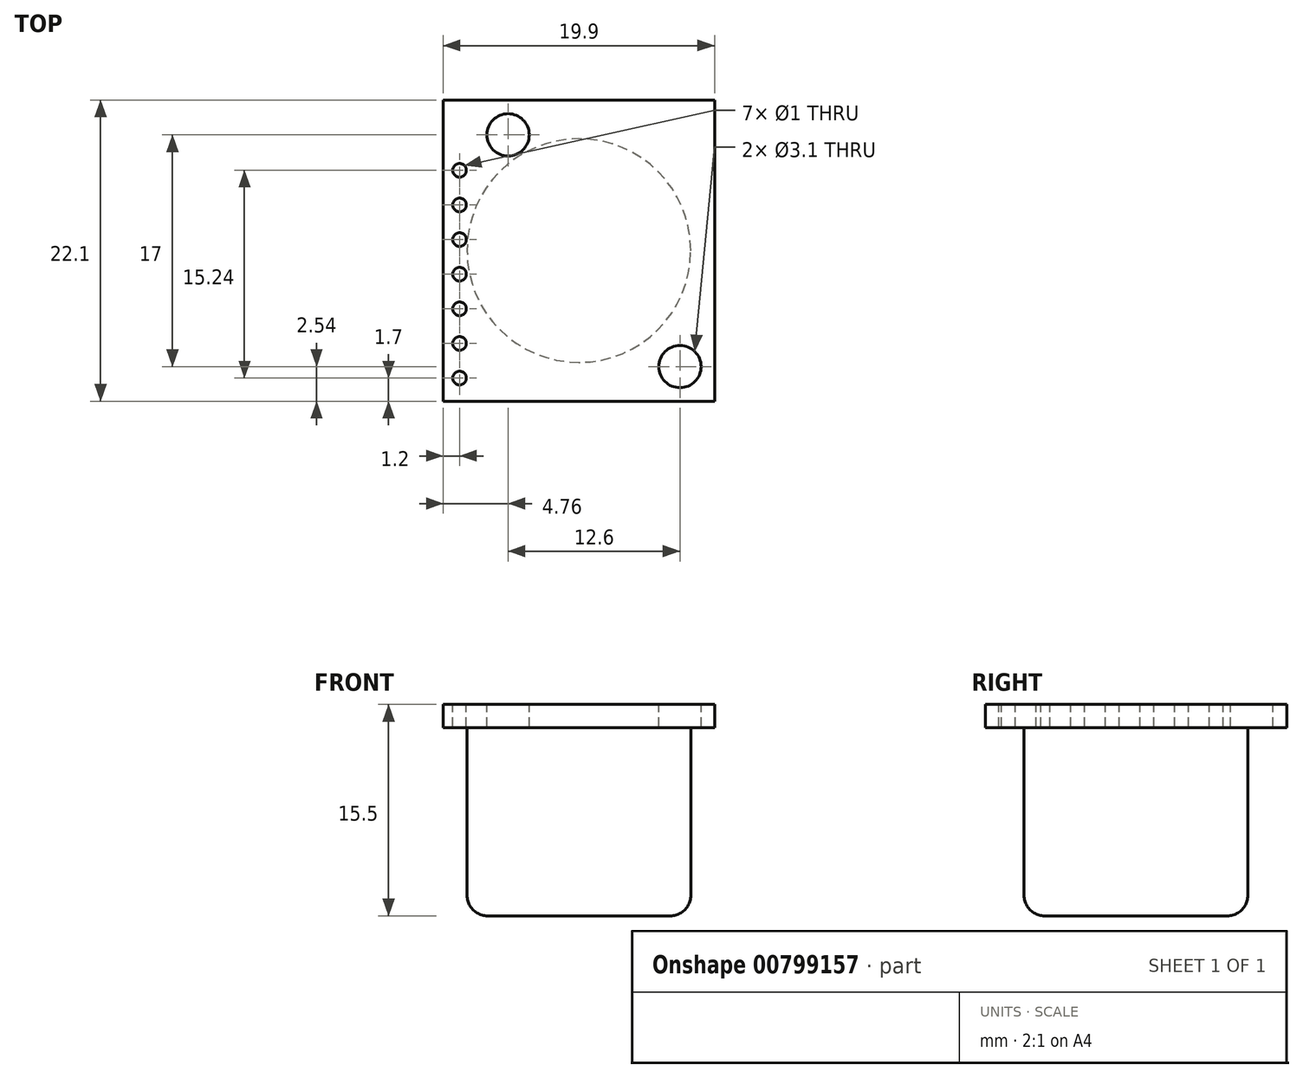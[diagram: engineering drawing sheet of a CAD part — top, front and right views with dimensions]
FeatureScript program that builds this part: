
annotation { "Feature Type Name" : "Feature", "Feature Type Description" : "" }
export const myFeature = defineFeature(function(context is Context, id is Id, definition is map)
    precondition{}
    {
        {
            var Q0;
            Q0=qCreatedBy(makeId("Top.planeOp"),FACE);
            var sketch = newSketch(context, id + "F0", { "sketchPlane" : qUnion([Q0])});
            skLineSegment(sketch, "E0.bottom", {"start": v(-9.95, 11.05) * mm, "end": v(9.95, 11.05) * mm});
            skLineSegment(sketch, "E0.top", {"start": v(-9.95, -11.05) * mm, "end": v(9.95, -11.05) * mm});
            skLineSegment(sketch, "E0.left", {"start": v(-9.95, 11.05) * mm, "end": v(-9.95, -11.05) * mm});
            skLineSegment(sketch, "E0.right", {"start": v(9.95, 11.05) * mm, "end": v(9.95, -11.05) * mm});
            skPoint(sketch, "E0.middle", {"position": v(0, 0) * mm});
            skPoint(sketch, "E1", {"position": v(7.41, -8.5) * mm});
            skPoint(sketch, "E2", {"position": v(-5.2, 8.5) * mm});
            skPoint(sketch, "E3", {"position": v(-8.75, -9.35) * mm});
            skPoint(sketch, "E4.0.1.0", {"position": v(-8.75, -6.81) * mm});
            skPoint(sketch, "E4.0.2.0", {"position": v(-8.75, -4.27) * mm});
            skPoint(sketch, "E4.0.3.0", {"position": v(-8.75, -1.73) * mm});
            skPoint(sketch, "E4.0.4.0", {"position": v(-8.75, 0.81) * mm});
            skPoint(sketch, "E4.0.5.0", {"position": v(-8.75, 3.35) * mm});
            skPoint(sketch, "E4.0.6.0", {"position": v(-8.75, 5.9) * mm});
            skLineSegment(sketch, "E4.direction1", {"start": v(-8.75, -9.35) * mm, "end": v(-8.75, -9.35) * mm});
            skLineSegment(sketch, "E4.direction2", {"start": v(-8.75, -9.35) * mm, "end": v(-8.75, -6.81) * mm, "construction": true});
            skSolve(sketch);
        }
        {
            var Q0;
            Q0=makeQuery(id+"F0.imprint","IMPRINT",FACE,{"disambiguationData":[TD([[makeQuery(id+"F0.imprint","IMPRINT",EDGE,{"derivedFrom":sQuery(id+"F0.wireOp",EDGE,"E0.bottom")}),-1.0]])]});
            extrude(context, id + "F1", {"entities" : qUnion([Q0]), "oppositeDirection" : true, "depth" : 1.7 * mm, "offsetDistance" : 25 * mm});
        }
        {
            var Q0;
            Q0=sQuery(id+"F0.wireOp",VERTEX,"E2");
            var Q1;
            Q1=sQuery(id+"F0.wireOp",VERTEX,"E1");
            var Q2;
            Q2=makeQuery(id+"F1.opExtrude","SWEPT_BODY",BODY,{"disambiguationData":[OSD([sQuery(id+"F0.wireOp",EDGE,"E0.bottom"),sQuery(id+"F0.wireOp",EDGE,"E0.top"),sQuery(id+"F0.wireOp",EDGE,"E0.left"),sQuery(id+"F0.wireOp",EDGE,"E0.right")])]});
            hole(context, id + "F2", {"style" : HoleStyle.SIMPLE, "endStyle" : HoleEndStyle.BLIND, "holeDiameter" : 3.1 * mm, "majorDiameter" : 5 * mm, "holeDepth" : 5 * mm, "isTappedThrough" : true, "tappedDepth" : 12 * mm, "tapClearance" : 3, "locations" : qUnion([Q0, Q1]), "scope" : qUnion([Q2])});
        }
        {
            var Q0;
            Q0=sQuery(id+"F0.wireOp",VERTEX,"E4.0.6.0");
            var Q1;
            Q1=sQuery(id+"F0.wireOp",VERTEX,"E4.0.5.0");
            var Q2;
            Q2=sQuery(id+"F0.wireOp",VERTEX,"E4.0.4.0");
            var Q3;
            Q3=sQuery(id+"F0.wireOp",VERTEX,"E4.0.3.0");
            var Q4;
            Q4=sQuery(id+"F0.wireOp",VERTEX,"E4.0.2.0");
            var Q5;
            Q5=sQuery(id+"F0.wireOp",VERTEX,"E4.0.1.0");
            var Q6;
            Q6=sQuery(id+"F0.wireOp",VERTEX,"E3");
            var Q7;
            Q7=makeQuery(id+"F1.opExtrude","SWEPT_BODY",BODY,{"disambiguationData":[OSD([sQuery(id+"F0.wireOp",EDGE,"E0.bottom"),sQuery(id+"F0.wireOp",EDGE,"E0.top"),sQuery(id+"F0.wireOp",EDGE,"E0.left"),sQuery(id+"F0.wireOp",EDGE,"E0.right")])]});
            hole(context, id + "F3", {"style" : HoleStyle.SIMPLE, "endStyle" : HoleEndStyle.BLIND, "holeDiameter" : 1 * mm, "majorDiameter" : 5 * mm, "holeDepth" : 5 * mm, "isTappedThrough" : true, "tappedDepth" : 12 * mm, "tapClearance" : 3, "locations" : qUnion([Q0, Q1, Q2, Q3, Q4, Q5, Q6]), "scope" : qUnion([Q7])});
        }
        {
            var Q0;
            Q0=makeQuery(id+"F1.opExtrude","CAP_FACE",FACE,{"disambiguationData":[OSD([sQuery(id+"F0.wireOp",EDGE,"E0.bottom"),sQuery(id+"F0.wireOp",EDGE,"E0.top"),sQuery(id+"F0.wireOp",EDGE,"E0.left"),sQuery(id+"F0.wireOp",EDGE,"E0.right")])],"isStart":false});
            var sketch = newSketch(context, id + "F4", { "sketchPlane" : qUnion([Q0])});
            skCircle(sketch, "E5", {"center": v(0, 0) * mm, "radius": 8.2 * mm});
            skSolve(sketch);
        }
        {
            var Q0;
            Q0=makeQuery(id+"F4.imprint","IMPRINT",FACE,{"disambiguationData":[TD([[makeQuery(id+"F4.imprint","IMPRINT",EDGE,{"derivedFrom":sQuery(id+"F4.wireOp",EDGE,"E5")}),1.0]])]});
            extrude(context, id + "F5", {"entities" : qUnion([Q0]), "operationType" : NewBodyOperationType.ADD, "depth" : (15.5 - 1.7) * mm, "offsetDistance" : 25 * mm});
        }
        {
            var Q0;
            Q0=makeQuery(id+"F5.opExtrude","CAP_EDGE",EDGE,{"disambiguationData":[OSD([sQuery(id+"F4.wireOp",EDGE,"E5")])],"isStart":false});
            fillet(context, id + "F6", {"entities" : qUnion([Q0]), "radius" : 1.5 * mm, "tangentPropagation" : true, "allowEdgeOverflow" : false});
        }
    });
